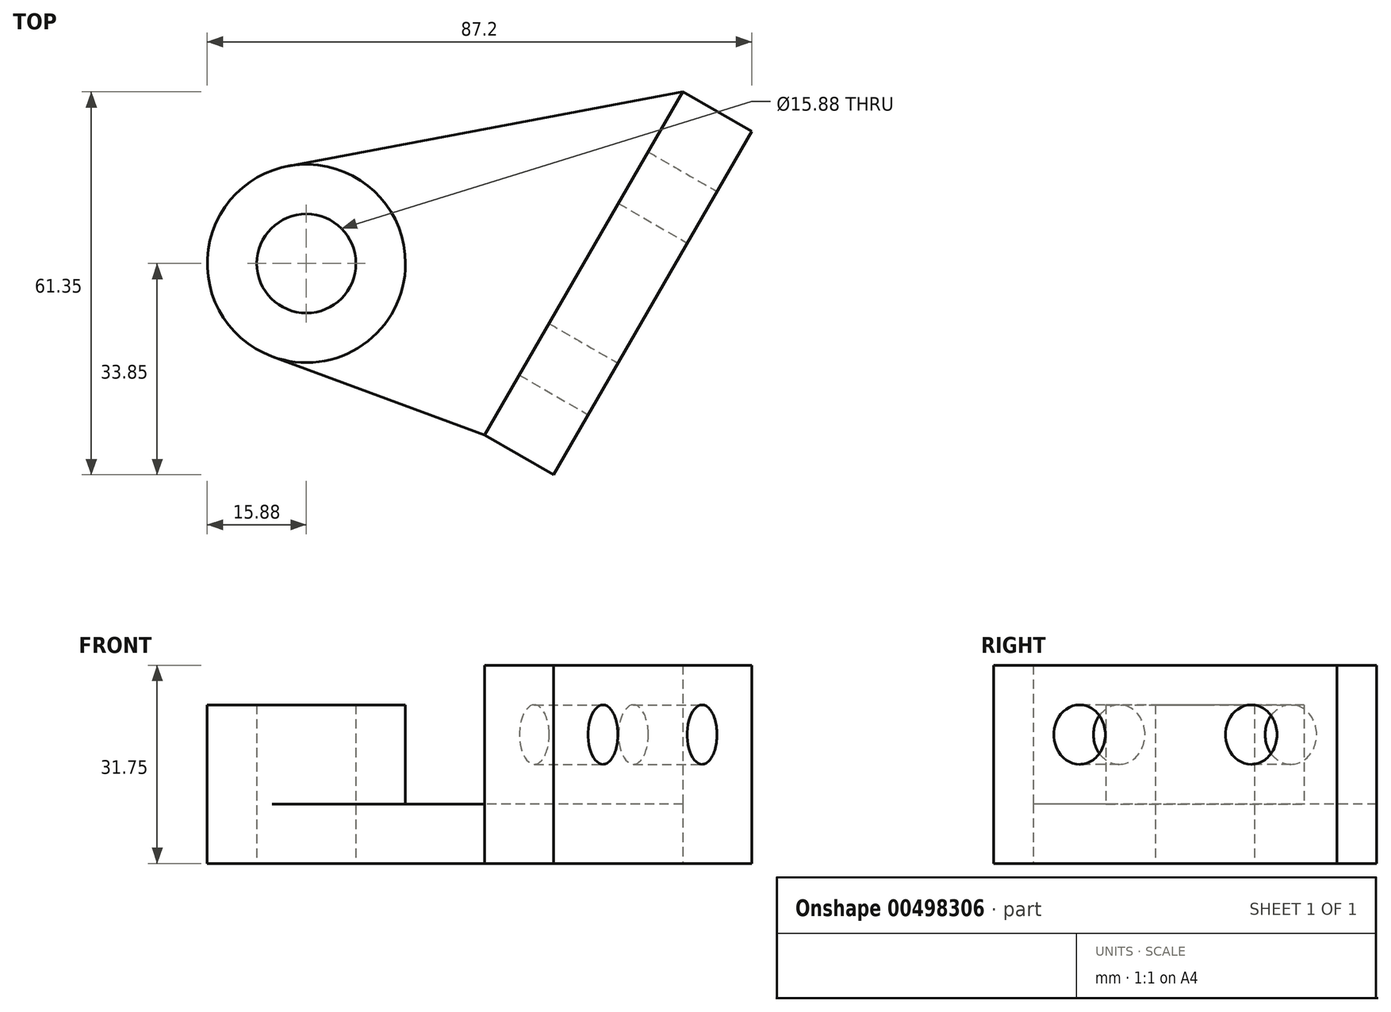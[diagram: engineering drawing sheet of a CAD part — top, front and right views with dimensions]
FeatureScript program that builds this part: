
annotation { "Feature Type Name" : "Feature", "Feature Type Description" : "" }
export const myFeature = defineFeature(function(context is Context, id is Id, definition is map)
    precondition{}
    {
        {
            var Q0;
            Q0=qCreatedBy(makeId("Top.planeOp"),FACE);
            var sketch = newSketch(context, id + "F0", { "sketchPlane" : qUnion([Q0])});
            skCircle(sketch, "E0", {"center": v(0, 0) * mm, "radius": 15.88 * mm});
            skCircle(sketch, "E1", {"center": v(0, 0) * mm, "radius": 7.94 * mm});
            skLineSegment(sketch, "E2", {"start": v(-29.1, 0) * mm, "end": v(78.42, 0) * mm, "construction": true});
            skLineSegment(sketch, "E3", {"start": v(44.45, -23.64) * mm, "end": v(44.45, 60.35) * mm, "construction": true});
            skLineSegment(sketch, "E4", {"start": v(60.32, 27.5) * mm, "end": v(28.58, -27.5) * mm});
            skPoint(sketch, "E5", {"position": v(44.45, 0) * mm});
            skLineSegment(sketch, "E6.0", {"start": v(71.32, 21.15) * mm, "end": v(39.57, -33.85) * mm});
            skLineSegment(sketch, "E7", {"start": v(60.33, 27.5) * mm, "end": v(71.32, 21.15) * mm});
            skLineSegment(sketch, "E8", {"start": v(28.58, -27.5) * mm, "end": v(39.57, -33.85) * mm});
            skLineSegment(sketch, "E9", {"start": v(60.33, 27.5) * mm, "end": v(-2.93, 15.6) * mm});
            skLineSegment(sketch, "E10", {"start": v(-5.5, -14.89) * mm, "end": v(28.58, -27.5) * mm});
            skSolve(sketch);
        }
        {
            var Q0;
            Q0=makeQuery(id+"F0.imprint","IMPRINT",FACE,{"disambiguationData":[TD([[makeQuery(id+"F0.imprint","IMPRINT",EDGE,{"derivedFrom":sQuery(id+"F0.wireOp",EDGE,"E4")}),-1.0]])]});
            extrude(context, id + "F1", {"entities" : qUnion([Q0]), "depth" : 9.52 * mm, "offsetDistance" : 25.4 * mm});
        }
        {
            var Q0;
            Q0=makeQuery(id+"F0.imprint","IMPRINT",FACE,{"disambiguationData":[TD([[makeQuery(id+"F0.imprint","IMPRINT",EDGE,{"derivedFrom":sQuery(id+"F0.wireOp",EDGE,"E1")}),-1.0]])]});
            extrude(context, id + "F2", {"entities" : qUnion([Q0]), "operationType" : NewBodyOperationType.ADD, "depth" : 25.4 * mm, "offsetDistance" : 25.4 * mm});
        }
        {
            var Q0;
            Q0=makeQuery(id+"F0.imprint","IMPRINT",FACE,{"disambiguationData":[TD([[makeQuery(id+"F0.imprint","IMPRINT",EDGE,{"derivedFrom":sQuery(id+"F0.wireOp",EDGE,"E4")}),1.0]])]});
            extrude(context, id + "F3", {"entities" : qUnion([Q0]), "operationType" : NewBodyOperationType.ADD, "depth" : 31.75 * mm, "offsetDistance" : 25.4 * mm});
        }
        {
            var Q0;
            Q0=makeQuery(id+"F3.opExtrude","SWEPT_FACE",FACE,{"disambiguationData":[OSD([sQuery(id+"F0.wireOp",EDGE,"E6.0")])]});
            var sketch = newSketch(context, id + "F4", { "sketchPlane" : qUnion([Q0])});
            skCircle(sketch, "E11", {"center": v(6.35, 20.64) * mm, "radius": 4.76 * mm});
            skCircle(sketch, "E12", {"center": v(38.1, 20.64) * mm, "radius": 4.76 * mm});
            skSolve(sketch);
        }
        {
            var Q0;
            Q0=makeQuery(id+"F4.imprint","IMPRINT",FACE,{"disambiguationData":[TD([[makeQuery(id+"F4.imprint","IMPRINT",EDGE,{"derivedFrom":sQuery(id+"F4.wireOp",EDGE,"E11")}),1.0]])]});
            var Q1;
            Q1=makeQuery(id+"F4.imprint","IMPRINT",FACE,{"disambiguationData":[TD([[makeQuery(id+"F4.imprint","IMPRINT",EDGE,{"derivedFrom":sQuery(id+"F4.wireOp",EDGE,"E12")}),1.0]])]});
            extrude(context, id + "F5", {"entities" : qUnion([Q0, Q1]), "operationType" : NewBodyOperationType.REMOVE, "oppositeDirection" : true, "depth" : 12.7 * mm, "offsetDistance" : 25.4 * mm});
        }
    });
